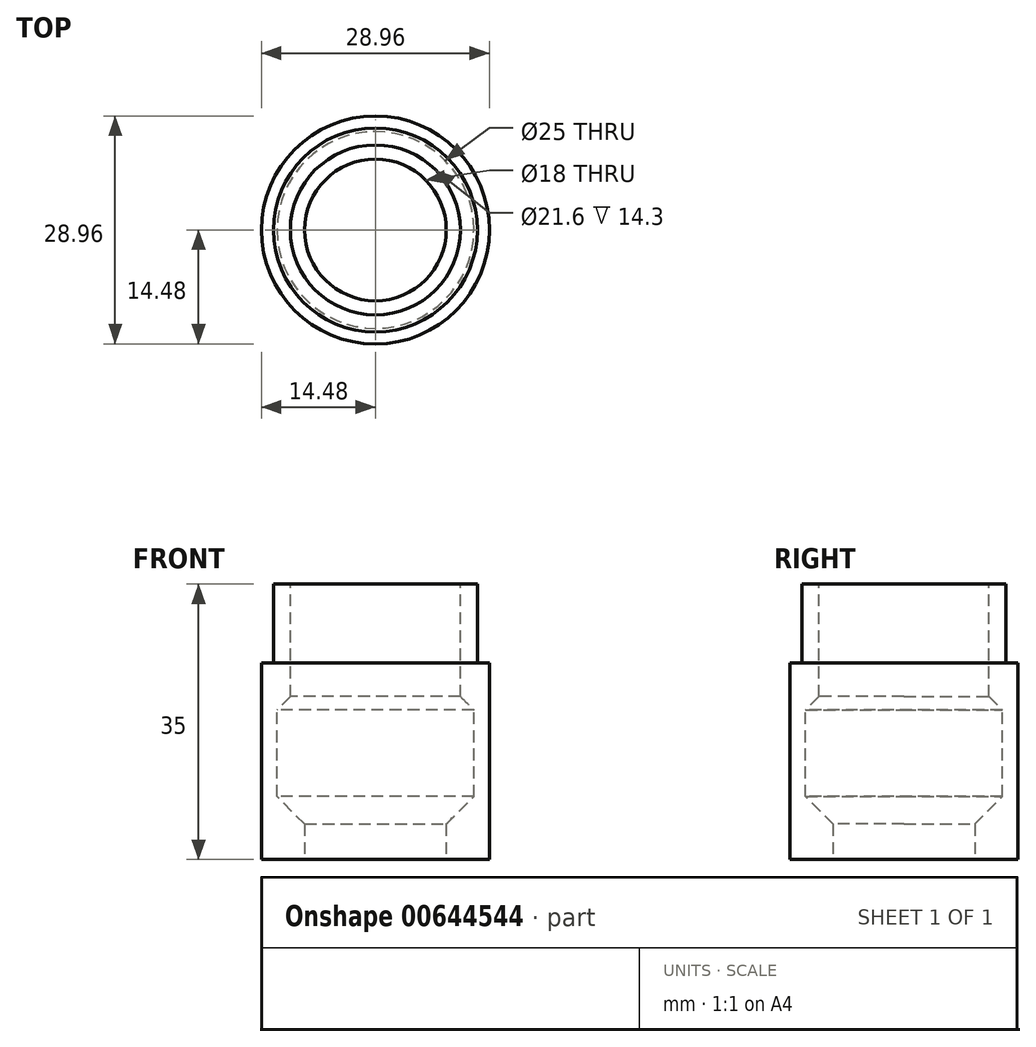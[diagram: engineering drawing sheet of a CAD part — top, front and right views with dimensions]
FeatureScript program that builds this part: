
annotation { "Feature Type Name" : "Feature", "Feature Type Description" : "" }
export const myFeature = defineFeature(function(context is Context, id is Id, definition is map)
    precondition{}
    {
        {
            var Q0;
            Q0=qCreatedBy(makeId("Top.planeOp"),FACE);
            var sketch = newSketch(context, id + "F0", { "sketchPlane" : qUnion([Q0])});
            skCircle(sketch, "E0", {"center": v(0, 0) * mm, "radius": 14.48 * mm});
            skSolve(sketch);
        }
        {
            var Q0;
            Q0 = qSketchRegion(id + "F0", true);
            extrude(context, id + "F1", {"entities" : qUnion([Q0]), "depth" : 25 * mm, "offsetDistance" : 25 * mm});
        }
        {
            var Q0;
            Q0=makeQuery(id+"F1.opExtrude","CAP_FACE",FACE,{"disambiguationData":[OSD([sQuery(id+"F0.wireOp",EDGE,"E0")])],"isStart":false});
            var sketch = newSketch(context, id + "F2", { "sketchPlane" : qUnion([Q0])});
            skCircle(sketch, "E1", {"center": v(0, 0) * mm, "radius": 12.5 * mm});
            skSolve(sketch);
        }
        {
            var Q0;
            Q0 = qSketchRegion(id + "F2", true);
            extrude(context, id + "F3", {"entities" : qUnion([Q0]), "operationType" : NewBodyOperationType.REMOVE, "oppositeDirection" : true, "depth" : 22 * mm, "offsetDistance" : 25 * mm});
        }
        {
            var Q0;
            Q0=makeQuery(id+"F1.opExtrude","CAP_FACE",FACE,{"disambiguationData":[OSD([sQuery(id+"F0.wireOp",EDGE,"E0")])],"isStart":true});
            var sketch = newSketch(context, id + "F4", { "sketchPlane" : qUnion([Q0])});
            skPoint(sketch, "E2.middle", {"position": v(0, 0) * mm});
            skCircle(sketch, "E3", {"center": v(0, 0) * mm, "radius": 9 * mm});
            skSolve(sketch);
        }
        {
            var Q0;
            Q0 = qSketchRegion(id + "F4", true);
            extrude(context, id + "F5", {"entities" : qUnion([Q0]), "operationType" : NewBodyOperationType.REMOVE, "endBound" : BoundingType.UP_TO_NEXT, "oppositeDirection" : true, "depth" : 25 * mm, "offsetDistance" : 25 * mm});
        }
        {
            var Q0;
            Q0=makeQuery(id+"F1.opExtrude","CAP_FACE",FACE,{"disambiguationData":[OSD([sQuery(id+"F0.wireOp",EDGE,"E0")])],"isStart":false});
            var sketch = newSketch(context, id + "F6", { "sketchPlane" : qUnion([Q0])});
            skCircle(sketch, "E4", {"center": v(0, 0) * mm, "radius": 12.5 * mm});
            skSolve(sketch);
        }
        {
            var Q0;
            Q0 = qSketchRegion(id + "F6", true);
            extrude(context, id + "F7", {"entities" : qUnion([Q0]), "operationType" : NewBodyOperationType.ADD, "oppositeDirection" : true, "depth" : 1 * mm, "offsetDistance" : 25 * mm});
        }
        {
            var Q0;
            Q0=makeQuery(id+"F7.boolean.opBoolean","MERGE",FACE,{"derivedFrom":[makeQuery(id+"F1.opExtrude","CAP_FACE",FACE,{"disambiguationData":[OSD([sQuery(id+"F0.wireOp",EDGE,"E0")])],"isStart":false}),makeQuery(id+"F7.opExtrude","CAP_FACE",FACE,{"disambiguationData":[OSD([sQuery(id+"F6.wireOp",EDGE,"E4")])],"isStart":true})]});
            var sketch = newSketch(context, id + "F8", { "sketchPlane" : qUnion([Q0])});
            skCircle(sketch, "E5", {"center": v(0, 0) * mm, "radius": 12.95 * mm});
            skSolve(sketch);
        }
        {
            var Q0;
            Q0 = qSketchRegion(id + "F8", true);
            extrude(context, id + "F9", {"entities" : qUnion([Q0]), "operationType" : NewBodyOperationType.ADD, "depth" : 10 * mm, "offsetDistance" : 25 * mm});
        }
        {
            var Q0;
            Q0=makeQuery(id+"F9.opExtrude","CAP_FACE",FACE,{"disambiguationData":[OSD([sQuery(id+"F8.wireOp",EDGE,"E5")])],"isStart":false});
            var sketch = newSketch(context, id + "F10", { "sketchPlane" : qUnion([Q0])});
            skCircle(sketch, "E6", {"center": v(0, 0) * mm, "radius": 10.8 * mm});
            skSolve(sketch);
        }
        {
            var Q0;
            Q0 = qSketchRegion(id + "F10", true);
            var Q1;
            Q1=makeQuery(id+"F7.opExtrude","CAP_FACE",FACE,{"disambiguationData":[OSD([sQuery(id+"F6.wireOp",EDGE,"E4")])],"isStart":false});
            extrude(context, id + "F11", {"entities" : qUnion([Q0]), "operationType" : NewBodyOperationType.REMOVE, "endBound" : BoundingType.UP_TO_SURFACE, "oppositeDirection" : true, "depth" : 25 * mm, "endBoundEntityFace" : qUnion([Q1]), "offsetDistance" : 25 * mm});
        }
        {
            var Q0;
            Q0=makeQuery(id+"F3.boolean.opBoolean","COPY",FACE,{"derivedFrom":makeQuery(id+"F3.opExtrude","SWEPT_FACE",FACE,{"disambiguationData":[OSD([sQuery(id+"F2.wireOp",EDGE,"E1")])]})});
            chamfer(context, id + "F12", {"entities" : qUnion([Q0]), "width" : 5 * mm, "tangentPropagation" : true});
        }
    });
